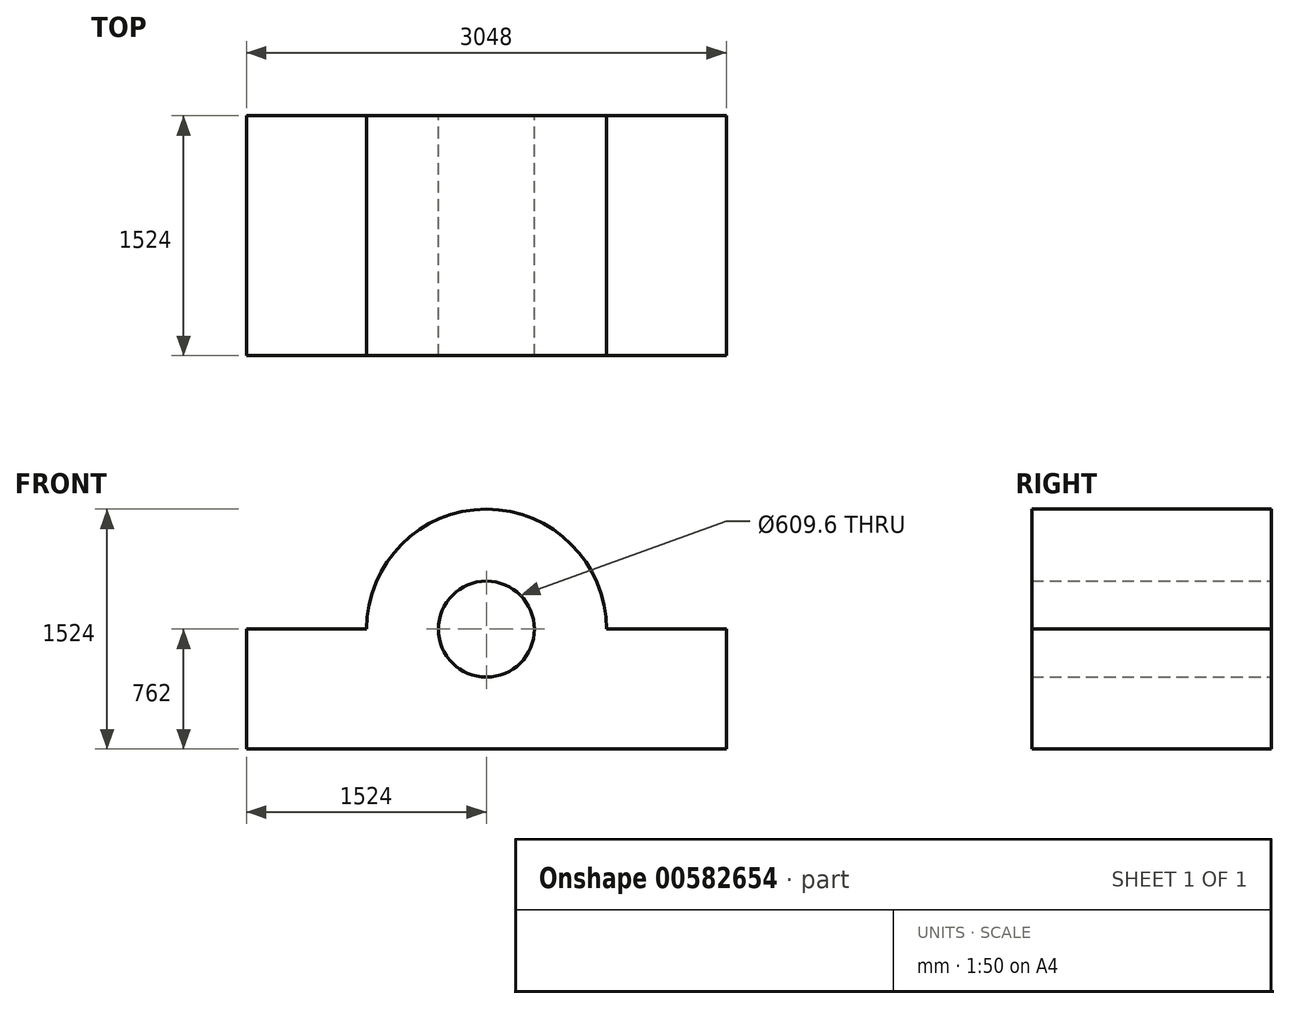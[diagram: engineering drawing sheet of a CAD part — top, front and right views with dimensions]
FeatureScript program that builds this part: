
annotation { "Feature Type Name" : "Feature", "Feature Type Description" : "" }
export const myFeature = defineFeature(function(context is Context, id is Id, definition is map)
    precondition{}
    {
        {
            var Q0;
            Q0=qCreatedBy(makeId("Front.planeOp"),FACE);
            var sketch = newSketch(context, id + "F0", { "sketchPlane" : qUnion([Q0])});
            skLineSegment(sketch, "E0", {"start": v(0, 0) * mm, "end": v(3048, 0) * mm});
            skLineSegment(sketch, "E1", {"start": v(0, 0) * mm, "end": v(0, 762) * mm});
            skLineSegment(sketch, "E2", {"start": v(3048, 0) * mm, "end": v(3048, 762) * mm});
            skPoint(sketch, "E3.orphan", {"position": v(1524, 0) * mm});
            skCircle(sketch, "E4", {"center": v(1524, 762) * mm, "radius": 304.8 * mm});
            skArc(sketch, "E5", {"start": v(2286, 762) * mm, "mid": v(1524, 1524) * mm, "end": v(762, 762) * mm});
            skLineSegment(sketch, "E6", {"start": v(0, 762) * mm, "end": v(762, 762) * mm});
            skLineSegment(sketch, "E7", {"start": v(3048, 762) * mm, "end": v(2286, 762) * mm});
            skSolve(sketch);
        }
        {
            var Q0;
            Q0=makeQuery(id+"F0.imprint","IMPRINT",FACE,{"disambiguationData":[TD([[makeQuery(id+"F0.imprint","IMPRINT",EDGE,{"derivedFrom":sQuery(id+"F0.wireOp",EDGE,"E0")}),1.0]])]});
            extrude(context, id + "F1", {"entities" : qUnion([Q0]), "depth" : 1524 * mm, "offsetDistance" : 25.4 * mm});
        }
    });
